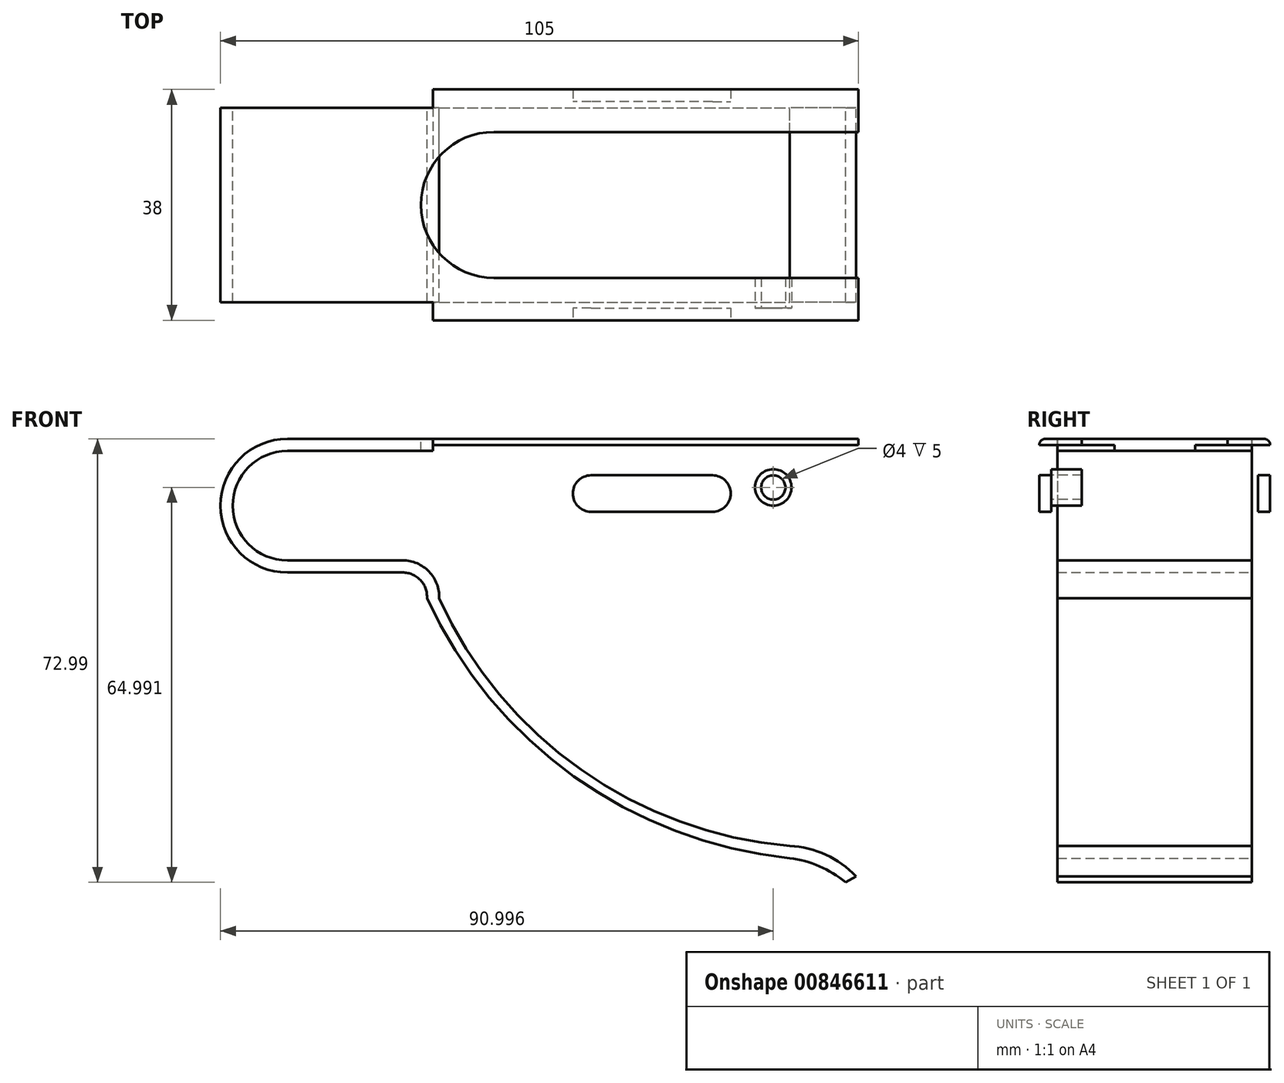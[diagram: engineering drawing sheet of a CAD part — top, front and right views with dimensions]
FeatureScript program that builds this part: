
annotation { "Feature Type Name" : "Feature", "Feature Type Description" : "" }
export const myFeature = defineFeature(function(context is Context, id is Id, definition is map)
    precondition{}
    {
        {
            var Q0;
            Q0=qCreatedBy(makeId("Front.planeOp"),FACE);
            var sketch = newSketch(context, id + "F0", { "sketchPlane" : qUnion([Q0])});
            skLineSegment(sketch, "E0.bottom", {"start": v(-47.71, 5.74) * mm, "end": v(46.29, 5.74) * mm});
            skLineSegment(sketch, "E0.top", {"start": v(-47.71, 3.74) * mm, "end": v(46.29, 3.74) * mm});
            skLineSegment(sketch, "E0.right", {"start": v(46.29, 5.74) * mm, "end": v(46.29, 3.74) * mm});
            skArc(sketch, "E1", {"start": v(-47.71, 3.74) * mm, "mid": v(-56.71, -5.26) * mm, "end": v(-47.71, -14.26) * mm});
            skLineSegment(sketch, "E2", {"start": v(-47.71, -14.26) * mm, "end": v(-28.71, -14.26) * mm});
            skArc(sketch, "E3", {"start": v(-22.72, -20.51) * mm, "mid": v(-24.38, -16.1) * mm, "end": v(-28.71, -14.26) * mm});
            skArc(sketch, "E4", {"start": v(-47.71, 5.74) * mm, "mid": v(-58.71, -5.26) * mm, "end": v(-47.71, -16.26) * mm});
            skLineSegment(sketch, "E5", {"start": v(-47.71, -16.26) * mm, "end": v(-28.71, -16.26) * mm});
            skArc(sketch, "E6", {"start": v(-24.72, -20.51) * mm, "mid": v(-25.8, -17.52) * mm, "end": v(-28.71, -16.26) * mm});
            skArc(sketch, "E7", {"start": v(-24.72, -20.51) * mm, "mid": v(-0.54, -49.82) * mm, "end": v(35, -63.26) * mm});
            skArc(sketch, "E8", {"start": v(-22.72, -20.51) * mm, "mid": v(0.62, -48.7) * mm, "end": v(35, -61.26) * mm});
            skArc(sketch, "E9", {"start": v(45.91, -66.26) * mm, "mid": v(40.94, -62.7) * mm, "end": v(35, -61.26) * mm});
            skArc(sketch, "E10", {"start": v(44.17, -67.25) * mm, "mid": v(39.87, -64.6) * mm, "end": v(35, -63.26) * mm});
            skLineSegment(sketch, "E11", {"start": v(44.17, -67.25) * mm, "end": v(45.91, -66.26) * mm});
            skSolve(sketch);
        }
        {
            var Q0;
            Q0=makeQuery(id+"F0.imprint","IMPRINT",FACE,{"disambiguationData":[TD([[makeQuery(id+"F0.imprint","IMPRINT",EDGE,{"derivedFrom":sQuery(id+"F0.wireOp",EDGE,"E0.bottom")}),-1.0]])]});
            extrude(context, id + "F1", {"entities" : qUnion([Q0]), "depth" : 16 * mm, "offsetDistance" : 25 * mm});
        }
        {
            var Q0;
            Q0=makeQuery(id+"F1.opExtrude","SWEPT_FACE",FACE,{"disambiguationData":[OSD([sQuery(id+"F0.wireOp",EDGE,"E0.bottom")])]});
            var sketch = newSketch(context, id + "F2", { "sketchPlane" : qUnion([Q0])});
            skLineSegment(sketch, "E12.bottom", {"start": v(46.29, -16) * mm, "end": v(-23.71, -16) * mm});
            skLineSegment(sketch, "E12.top", {"start": v(46.29, -19) * mm, "end": v(-23.71, -19) * mm});
            skLineSegment(sketch, "E12.left", {"start": v(46.29, -16) * mm, "end": v(46.29, -19) * mm});
            skLineSegment(sketch, "E12.right", {"start": v(-23.71, -16) * mm, "end": v(-23.71, -19) * mm});
            skSolve(sketch);
        }
        {
            var Q0;
            Q0=makeQuery(id+"F2.imprint","IMPRINT",FACE,{"disambiguationData":[TD([[makeQuery(id+"F2.imprint","IMPRINT",EDGE,{"derivedFrom":sQuery(id+"F2.wireOp",EDGE,"E12.bottom")}),-1.0]])]});
            extrude(context, id + "F3", {"entities" : qUnion([Q0]), "operationType" : NewBodyOperationType.ADD, "oppositeDirection" : true, "depth" : 2 * mm, "offsetDistance" : 25 * mm});
        }
        {
            var Q0;
            Q0=makeQuery(id+"F3.opExtrude","SWEPT_FACE",FACE,{"disambiguationData":[OSD([sQuery(id+"F2.wireOp",EDGE,"E12.top")])]});
            var sketch = newSketch(context, id + "F4", { "sketchPlane" : qUnion([Q0])});
            skLineSegment(sketch, "E13.bottom", {"start": v(46.29, 5.74) * mm, "end": v(-3.71, 5.74) * mm});
            skLineSegment(sketch, "E13.top", {"start": v(46.29, -8.26) * mm, "end": v(-3.71, -8.26) * mm});
            skLineSegment(sketch, "E13.left", {"start": v(46.29, 5.74) * mm, "end": v(46.29, -8.26) * mm});
            skLineSegment(sketch, "E13.right", {"start": v(-3.71, 5.74) * mm, "end": v(-3.71, -8.26) * mm});
            skSolve(sketch);
        }
        {
            var Q0;
            {var subQ0=sQuery(id+"F4.wireOp",EDGE,"E13.top");Q0=makeQuery(id+"F4.imprint","IMPRINT",FACE,{"disambiguationData":[TD([[makeQuery(id+"F4.imprint","IMPRINT",EDGE,{"derivedFrom":subQ0}),-1.0]])]});}
            extrude(context, id + "F5", {"entities" : qUnion([Q0]), "operationType" : NewBodyOperationType.ADD, "oppositeDirection" : true, "depth" : 2 * mm, "offsetDistance" : 25 * mm});
        }
        {
            var Q0;
            Q0=makeQuery(id+"F3.opExtrude","CAP_EDGE",EDGE,{"disambiguationData":[OSD([sQuery(id+"F2.wireOp",EDGE,"E12.top")])],"isStart":true});
            var Q1;
            Q1=makeQuery(id+"F5.opExtrude","CAP_EDGE",EDGE,{"disambiguationData":[OSD([sQuery(id+"F2.wireOp",EDGE,"E12.top")])],"isStart":false});
            fillet(context, id + "F6", {"entities" : qUnion([Q0, Q1]), "radius" : 1 * mm, "tangentPropagation" : true, "allowEdgeOverflow" : false});
        }
        {
            var Q0;
            Q0=makeQuery(id+"F1.opExtrude","SWEPT_BODY",BODY,{"disambiguationData":[OSD([sQuery(id+"F0.wireOp",EDGE,"E0.bottom"),sQuery(id+"F0.wireOp",EDGE,"E0.top"),sQuery(id+"F0.wireOp",EDGE,"E0.right"),sQuery(id+"F0.wireOp",EDGE,"E1"),sQuery(id+"F0.wireOp",EDGE,"E2"),sQuery(id+"F0.wireOp",EDGE,"E3"),sQuery(id+"F0.wireOp",EDGE,"E4"),sQuery(id+"F0.wireOp",EDGE,"E5"),sQuery(id+"F0.wireOp",EDGE,"E6"),sQuery(id+"F0.wireOp",EDGE,"E7"),sQuery(id+"F0.wireOp",EDGE,"E8"),sQuery(id+"F0.wireOp",EDGE,"E9"),sQuery(id+"F0.wireOp",EDGE,"E10"),sQuery(id+"F0.wireOp",EDGE,"E11")])]});
            var Q1;
            Q1=qCreatedBy(makeId("Front.planeOp"),FACE);
            mirror(context, id + "F7", {"operationType" : NewBodyOperationType.ADD, "entities" : qUnion([Q0]), "mirrorPlane" : qUnion([Q1])});
        }
        {
            var Q0;
            {var subQ0=makeQuery(id+"F3.boolean.opBoolean","MERGE",FACE,{"derivedFrom":[makeQuery(id+"F1.opExtrude","SWEPT_FACE",FACE,{"disambiguationData":[OSD([sQuery(id+"F0.wireOp",EDGE,"E0.bottom")])]}),makeQuery(id+"F3.opExtrude","CAP_FACE",FACE,{"disambiguationData":[OSD([sQuery(id+"F2.wireOp",EDGE,"E12.bottom"),sQuery(id+"F2.wireOp",EDGE,"E12.top"),sQuery(id+"F2.wireOp",EDGE,"E12.left"),sQuery(id+"F2.wireOp",EDGE,"E12.right")])],"isStart":true})]});Q0=makeQuery(id+"F7.boolean.opBoolean","MERGE",FACE,{"derivedFrom":[subQ0,makeQuery(id+"F7.opPattern","COPY",FACE,{"derivedFrom":subQ0,"instanceName":"1"})]});}
            var sketch = newSketch(context, id + "F8", { "sketchPlane" : qUnion([Q0])});
            skArc(sketch, "E14", {"start": v(-13.71, 12) * mm, "mid": v(-25.71, 0) * mm, "end": v(-13.71, -12) * mm});
            skLineSegment(sketch, "E15", {"start": v(-13.71, -12) * mm, "end": v(46.29, -12) * mm});
            skLineSegment(sketch, "E16", {"start": v(-13.71, 12) * mm, "end": v(46.29, 12) * mm});
            skLineSegment(sketch, "E17", {"start": v(46.29, 12) * mm, "end": v(46.29, -12) * mm});
            skSolve(sketch);
        }
        {
            var Q0;
            Q0=makeQuery(id+"F8.imprint","IMPRINT",FACE,{"disambiguationData":[TD([[makeQuery(id+"F8.imprint","IMPRINT",EDGE,{"derivedFrom":sQuery(id+"F8.wireOp",EDGE,"E14")}),1.0]])]});
            extrude(context, id + "F9", {"entities" : qUnion([Q0]), "operationType" : NewBodyOperationType.REMOVE, "oppositeDirection" : true, "depth" : 2 * mm, "offsetDistance" : 25 * mm});
        }
        {
            var Q0;
            {var subQ0=sQuery(id+"F2.wireOp",EDGE,"E12.top");Q0=makeQuery(id+"F5.boolean.opBoolean","MERGE",FACE,{"derivedFrom":[makeQuery(id+"F3.opExtrude","SWEPT_FACE",FACE,{"disambiguationData":[OSD([subQ0])]}),makeQuery(id+"F5.opExtrude","CAP_FACE",FACE,{"disambiguationData":[OSD([subQ0,sQuery(id+"F4.wireOp",EDGE,"E13.top"),sQuery(id+"F4.wireOp",EDGE,"E13.left"),sQuery(id+"F4.wireOp",EDGE,"E13.right")])],"isStart":true})]});}
            var sketch = newSketch(context, id + "F10", { "sketchPlane" : qUnion([Q0])});
            skLineSegment(sketch, "E18", {"start": v(2.29, -3.26) * mm, "end": v(22.29, -3.26) * mm});
            skArc(sketch, "E19.0.startCap", {"start": v(2.29, -6.26) * mm, "mid": v(-0.71, -3.26) * mm, "end": v(2.29, -0.26) * mm});
            skArc(sketch, "E19.0.endCap", {"start": v(22.29, -0.26) * mm, "mid": v(25.29, -3.26) * mm, "end": v(22.29, -6.26) * mm});
            skLineSegment(sketch, "E19.0.left", {"start": v(2.29, -0.26) * mm, "end": v(22.29, -0.26) * mm});
            skLineSegment(sketch, "E19.0.right", {"start": v(2.29, -6.26) * mm, "end": v(22.29, -6.26) * mm});
            skSolve(sketch);
        }
        {
            var Q0;
            Q0=makeQuery(id+"F10.imprint","IMPRINT",FACE,{"disambiguationData":[TD([[makeQuery(id+"F10.imprint","IMPRINT",EDGE,{"derivedFrom":sQuery(id+"F10.wireOp",EDGE,"E19.0.startCap")}),-1.0]])]});
            extrude(context, id + "F11", {"entities" : qUnion([Q0]), "operationType" : NewBodyOperationType.REMOVE, "endBound" : BoundingType.THROUGH_ALL, "oppositeDirection" : true, "depth" : 25 * mm, "offsetDistance" : 25 * mm});
        }
        {
            var Q0;
            {var subQ0=sQuery(id+"F2.wireOp",EDGE,"E12.top");Q0=makeQuery(id+"F5.boolean.opBoolean","MERGE",FACE,{"derivedFrom":[makeQuery(id+"F3.opExtrude","SWEPT_FACE",FACE,{"disambiguationData":[OSD([subQ0])]}),makeQuery(id+"F5.opExtrude","CAP_FACE",FACE,{"disambiguationData":[OSD([subQ0,sQuery(id+"F4.wireOp",EDGE,"E13.top"),sQuery(id+"F4.wireOp",EDGE,"E13.left"),sQuery(id+"F4.wireOp",EDGE,"E13.right")])],"isStart":true})]});}
            var sketch = newSketch(context, id + "F12", { "sketchPlane" : qUnion([Q0])});
            skPoint(sketch, "E20", {"position": v(32.29, -2.26) * mm});
            skSolve(sketch);
        }
        {
            var Q0;
            Q0=sQuery(id+"F12.wireOp",VERTEX,"E20");
            var Q1;
            Q1=makeQuery(id+"F1.opExtrude","SWEPT_BODY",BODY,{"disambiguationData":[OSD([sQuery(id+"F0.wireOp",EDGE,"E0.bottom"),sQuery(id+"F0.wireOp",EDGE,"E0.top"),sQuery(id+"F0.wireOp",EDGE,"E0.right"),sQuery(id+"F0.wireOp",EDGE,"E1"),sQuery(id+"F0.wireOp",EDGE,"E2"),sQuery(id+"F0.wireOp",EDGE,"E3"),sQuery(id+"F0.wireOp",EDGE,"E4"),sQuery(id+"F0.wireOp",EDGE,"E5"),sQuery(id+"F0.wireOp",EDGE,"E6"),sQuery(id+"F0.wireOp",EDGE,"E7"),sQuery(id+"F0.wireOp",EDGE,"E8"),sQuery(id+"F0.wireOp",EDGE,"E9"),sQuery(id+"F0.wireOp",EDGE,"E10"),sQuery(id+"F0.wireOp",EDGE,"E11")])]});
            hole(context, id + "F13", {"style" : HoleStyle.SIMPLE, "endStyle" : HoleEndStyle.THROUGH, "holeDiameter" : 4 * mm, "majorDiameter" : 5 * mm, "isTappedThrough" : true, "tappedDepth" : 12 * mm, "tapClearance" : 3, "locations" : qUnion([Q0]), "scope" : qUnion([Q1])});
        }
        {
            var Q0;
            Q0=makeQuery(id+"F5.opExtrude","CAP_FACE",FACE,{"disambiguationData":[OSD([sQuery(id+"F2.wireOp",EDGE,"E12.top"),sQuery(id+"F4.wireOp",EDGE,"E13.top"),sQuery(id+"F4.wireOp",EDGE,"E13.left"),sQuery(id+"F4.wireOp",EDGE,"E13.right")])],"isStart":false});
            var sketch = newSketch(context, id + "F14", { "sketchPlane" : qUnion([Q0])});
            skCircle(sketch, "E21.0", {"center": v(-32.29, -2.26) * mm, "radius": 2 * mm});
            skCircle(sketch, "E22.0", {"center": v(-32.29, -2.26) * mm, "radius": 3 * mm});
            skSolve(sketch);
        }
        {
            var Q0;
            Q0=makeQuery(id+"F14.imprint","IMPRINT",FACE,{"disambiguationData":[TD([[makeQuery(id+"F14.imprint","IMPRINT",EDGE,{"derivedFrom":sQuery(id+"F14.wireOp",EDGE,"E21.0")}),-1.0]])]});
            extrude(context, id + "F15", {"entities" : qUnion([Q0]), "operationType" : NewBodyOperationType.ADD, "depth" : 5 * mm, "offsetDistance" : 25 * mm});
        }
    });
